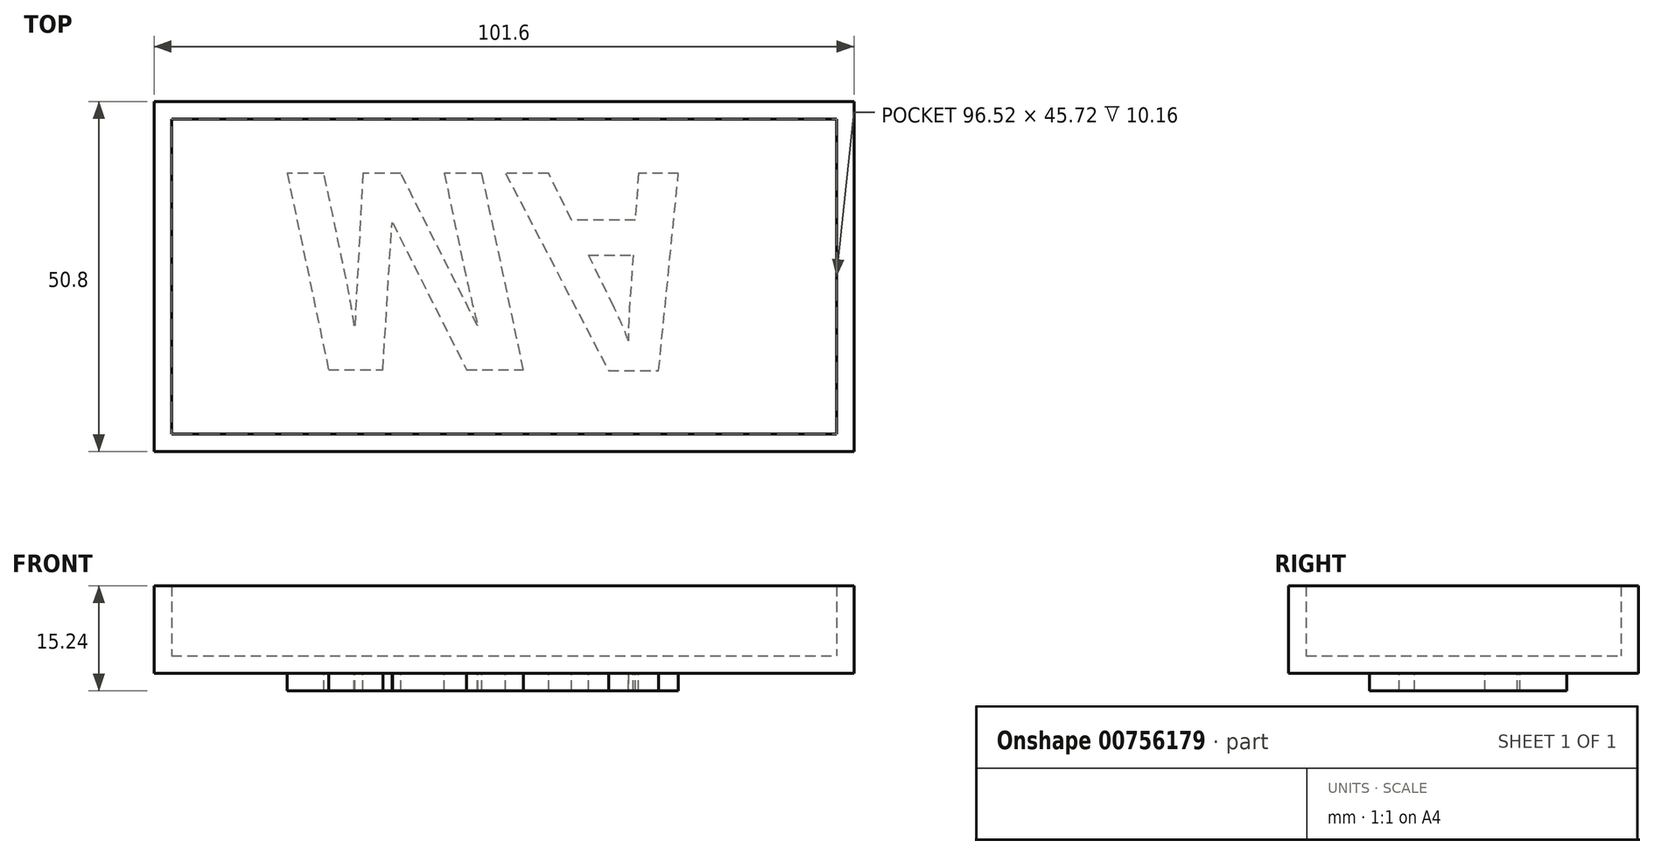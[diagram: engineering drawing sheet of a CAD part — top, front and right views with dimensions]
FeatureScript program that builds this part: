
annotation { "Feature Type Name" : "Feature", "Feature Type Description" : "" }
export const myFeature = defineFeature(function(context is Context, id is Id, definition is map)
    precondition{}
    {
        {
            var Q0;
            Q0=qCreatedBy(makeId("Top.planeOp"),FACE);
            var sketch = newSketch(context, id + "F0", { "sketchPlane" : qUnion([Q0])});
            skLineSegment(sketch, "E0.bottom", {"start": v(-50.8, -25.4) * mm, "end": v(50.8, -25.4) * mm});
            skLineSegment(sketch, "E0.top", {"start": v(-50.8, 25.4) * mm, "end": v(50.8, 25.4) * mm});
            skLineSegment(sketch, "E0.left", {"start": v(-50.8, -25.4) * mm, "end": v(-50.8, 25.4) * mm});
            skLineSegment(sketch, "E0.right", {"start": v(50.8, -25.4) * mm, "end": v(50.8, 25.4) * mm});
            skPoint(sketch, "E0.middle", {"position": v(0, 0) * mm});
            skSolve(sketch);
        }
        {
            var Q0;
            Q0=makeQuery(id+"F0.imprint","IMPRINT",FACE,{"disambiguationData":[TD([[makeQuery(id+"F0.imprint","IMPRINT",EDGE,{"derivedFrom":sQuery(id+"F0.wireOp",EDGE,"E0.bottom")}),1.0]])]});
            extrude(context, id + "F1", {"entities" : qUnion([Q0]), "depth" : 12.7 * mm, "offsetDistance" : 25.4 * mm});
        }
        {
            var Q0;
            Q0=makeQuery(id+"F1.opExtrude","CAP_FACE",FACE,{"disambiguationData":[OSD([sQuery(id+"F0.wireOp",EDGE,"E0.bottom"),sQuery(id+"F0.wireOp",EDGE,"E0.top"),sQuery(id+"F0.wireOp",EDGE,"E0.left"),sQuery(id+"F0.wireOp",EDGE,"E0.right")])],"isStart":false});
            shell(context, id + "F2", {"entities" : qUnion([Q0]), "thickness" : 2.54 * mm});
        }
        {
            var Q0;
            Q0=makeQuery(id+"F1.opExtrude","CAP_FACE",FACE,{"disambiguationData":[OSD([sQuery(id+"F0.wireOp",EDGE,"E0.bottom"),sQuery(id+"F0.wireOp",EDGE,"E0.top"),sQuery(id+"F0.wireOp",EDGE,"E0.left"),sQuery(id+"F0.wireOp",EDGE,"E0.right")])],"isStart":true});
            var sketch = newSketch(context, id + "F3", { "sketchPlane" : qUnion([Q0])});
            skText(sketch, "E1", { "text": "MA", "fontName": "OpenSans-BoldItalic.ttf"});
            const initialGuessF3  = {"E1": [-0.03252, -0.015, 1, 0, 0.02877]};
            skSetInitialGuess(sketch, initialGuessF3);
            skSolve(sketch);
        }
        {
            var Q0;
            Q0 = qSketchRegion(id + "F3", true);
            extrude(context, id + "F4", {"entities" : qUnion([Q0]), "operationType" : NewBodyOperationType.ADD, "depth" : 2.54 * mm, "offsetDistance" : 25.4 * mm});
        }
    });
